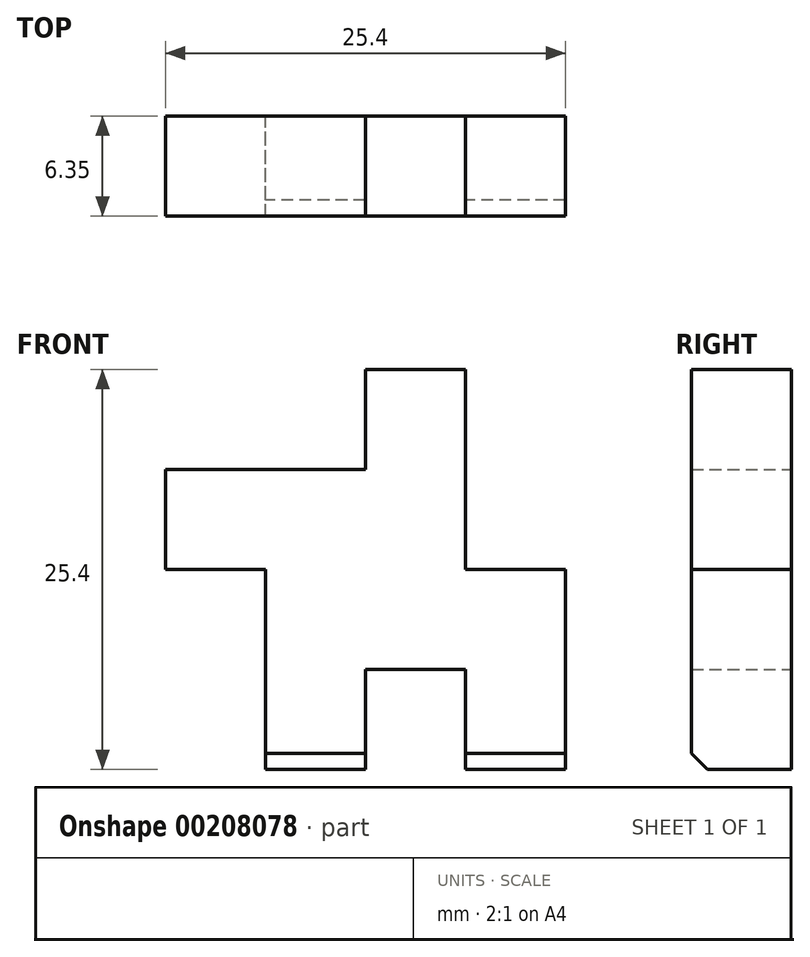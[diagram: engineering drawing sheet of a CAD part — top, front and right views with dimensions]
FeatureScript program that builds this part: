
annotation { "Feature Type Name" : "Feature", "Feature Type Description" : "" }
export const myFeature = defineFeature(function(context is Context, id is Id, definition is map)
    precondition{}
    {
        {
            var Q0;
            Q0=qCreatedBy(makeId("Front.planeOp"),FACE);
            var sketch = newSketch(context, id + "F0", { "sketchPlane" : qUnion([Q0])});
            skLineSegment(sketch, "E0.bottom", {"start": v(6.35, 12.7) * mm, "end": v(0, 12.7) * mm});
            skLineSegment(sketch, "E0.top", {"start": v(12.7, -12.7) * mm, "end": v(6.35, -12.7) * mm});
            skLineSegment(sketch, "E0.left", {"start": v(12.7, 0) * mm, "end": v(12.7, -12.7) * mm});
            skLineSegment(sketch, "E0.right", {"start": v(-12.7, 12.7) * mm, "end": v(-12.7, 0) * mm});
            skPoint(sketch, "E0.middle", {"position": v(0, 0) * mm});
            skLineSegment(sketch, "E1", {"start": v(-12.7, 0) * mm, "end": v(-6.35, 0) * mm});
            skLineSegment(sketch, "E2", {"start": v(-6.35, 0) * mm, "end": v(-6.35, -12.7) * mm});
            skLineSegment(sketch, "E3", {"start": v(0, 12.7) * mm, "end": v(0, 6.35) * mm});
            skPoint(sketch, "E3.endSnap0", {"position": v(0, 12.7) * mm});
            skLineSegment(sketch, "E4", {"start": v(0, 6.35) * mm, "end": v(-12.7, 6.35) * mm});
            skLineSegment(sketch, "E5", {"start": v(6.35, 12.7) * mm, "end": v(6.35, 0) * mm});
            skPoint(sketch, "E6.orphan", {"position": v(6.35, 14) * mm});
            skLineSegment(sketch, "E7", {"start": v(6.35, 0) * mm, "end": v(12.7, 0) * mm});
            skLineSegment(sketch, "E8", {"start": v(0, -6.35) * mm, "end": v(6.35, -6.35) * mm});
            skLineSegment(sketch, "E9", {"start": v(6.35, 0) * mm, "end": v(6.35, -12.7) * mm});
            skLineSegment(sketch, "E10", {"start": v(0, -6.35) * mm, "end": v(0, -12.7) * mm});
            skPoint(sketch, "E10.endSnap0", {"position": v(0, -12.7) * mm});
            skPoint(sketch, "E11.orphan", {"position": v(0, -14.52) * mm});
            skPoint(sketch, "E12.orphan", {"position": v(12.7, 12.7) * mm});
            skLineSegment(sketch, "E13.trimOffspring", {"start": v(0, -12.7) * mm, "end": v(-6.35, -12.7) * mm});
            skPoint(sketch, "E14.orphan", {"position": v(-12.7, -12.7) * mm});
            skPoint(sketch, "E15.orphan", {"position": v(-6.35, -6.35) * mm});
            skSolve(sketch);
        }
        {
            var Q0;
            Q0 = qSketchRegion(id + "F0", true);
            extrude(context, id + "F1", {"entities" : qUnion([Q0]), "depth" : 6.35 * mm});
        }
        {
            var Q0;
            Q0=makeQuery(id+"F1.opExtrude","CAP_EDGE",EDGE,{"disambiguationData":[OSD([sQuery(id+"F0.wireOp",EDGE,"E13.trimOffspring")])],"isStart":false});
            var Q1;
            Q1=makeQuery(id+"F1.opExtrude","CAP_EDGE",EDGE,{"disambiguationData":[OSD([sQuery(id+"F0.wireOp",EDGE,"E0.top")])],"isStart":false});
            chamfer(context, id + "F2", {"entities" : qUnion([Q0, Q1]), "width" : 1.02 * mm, "tangentPropagation" : true});
        }
    });
